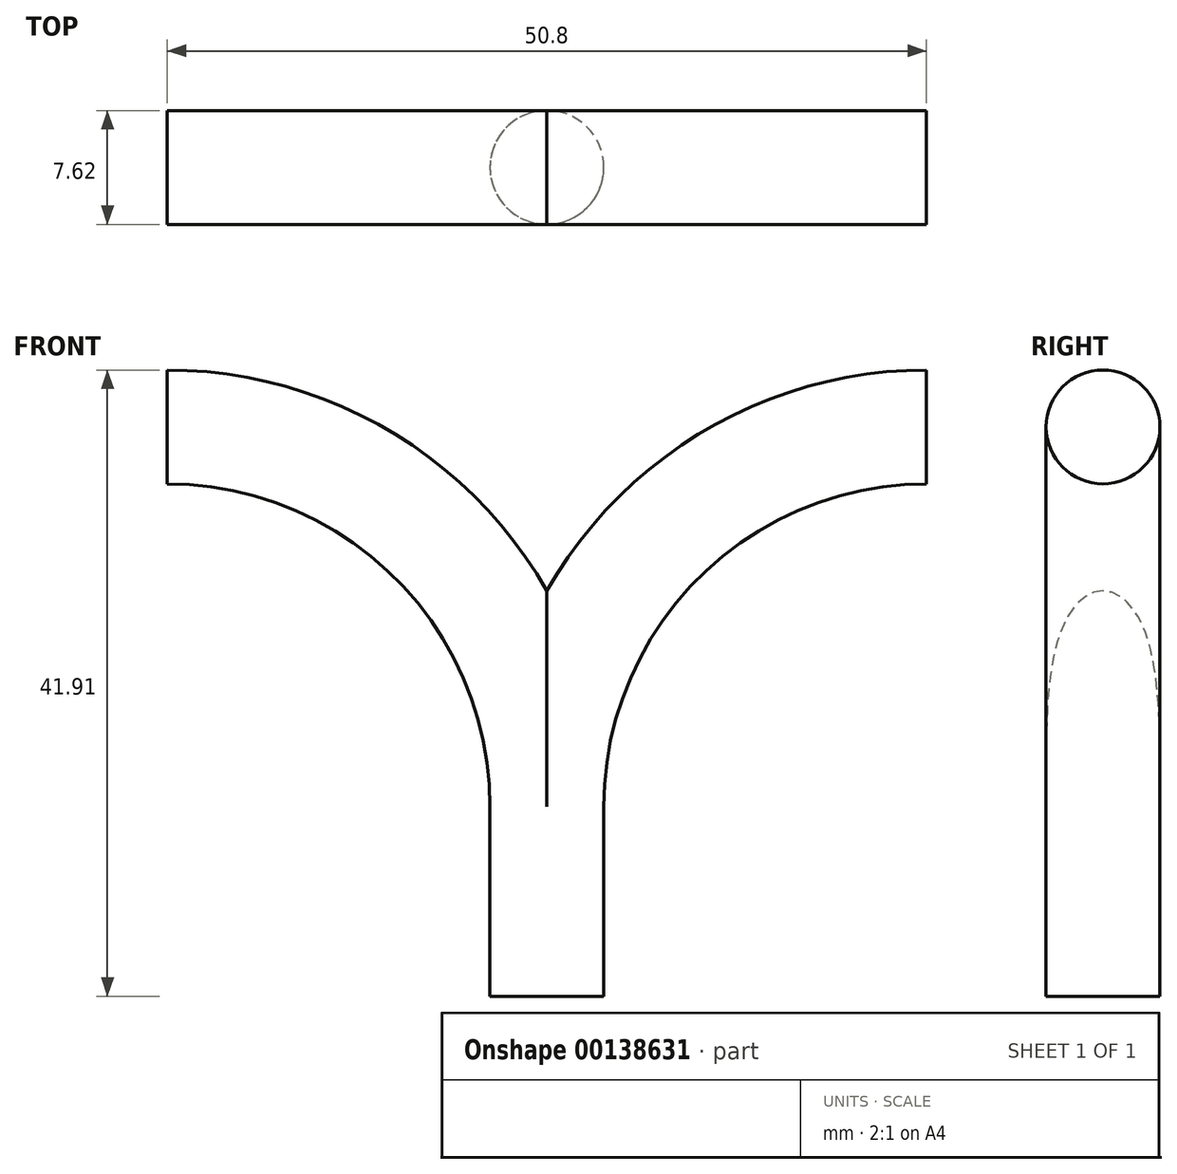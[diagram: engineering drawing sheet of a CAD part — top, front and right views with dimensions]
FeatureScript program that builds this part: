
annotation { "Feature Type Name" : "Feature", "Feature Type Description" : "" }
export const myFeature = defineFeature(function(context is Context, id is Id, definition is map)
    precondition{}
    {
        {
            var Q0;
            Q0=qCreatedBy(makeId("Top.planeOp"),FACE);
            var sketch = newSketch(context, id + "F0", { "sketchPlane" : qUnion([Q0])});
            skCircle(sketch, "E0", {"center": v(0, 0) * mm, "radius": 3.81 * mm});
            skSolve(sketch);
        }
        {
            var Q0;
            Q0=qCreatedBy(makeId("Front.planeOp"),FACE);
            var sketch = newSketch(context, id + "F1", { "sketchPlane" : qUnion([Q0])});
            skArc(sketch, "E1", {"start": v(0, 0) * mm, "mid": v(-7.44, 17.96) * mm, "end": v(-25.4, 25.4) * mm});
            skArc(sketch, "E2", {"start": v(25.4, 25.4) * mm, "mid": v(7.44, 17.96) * mm, "end": v(0, 0) * mm});
            skSolve(sketch);
        }
        {
            var Q0;
            Q0=makeQuery(id+"F0.imprint","IMPRINT",FACE,{"disambiguationData":[TD([[makeQuery(id+"F0.imprint","IMPRINT",EDGE,{"derivedFrom":sQuery(id+"F0.wireOp",EDGE,"E0")}),1.0]])]});
            var Q1;
            Q1=sQuery(id+"F1.wireOp",EDGE,"E2");
            sweep(context, id + "F2", {"profiles" : qUnion([Q0]), "path" : qUnion([Q1])});
        }
        {
            var Q0;
            Q0 = qSketchRegion(id + "F0", true);
            var Q1;
            Q1=sQuery(id+"F1.wireOp",EDGE,"E1");
            sweep(context, id + "F3", {"operationType" : NewBodyOperationType.ADD, "profiles" : qUnion([Q0]), "path" : qUnion([Q1])});
        }
        {
            var Q0;
            Q0=makeQuery(id+"F2.opSweep","CAP_FACE",FACE,{"disambiguationData":[OSD([sQuery(id+"F0.wireOp",EDGE,"E0"),sQuery(id+"F1.wireOp",VERTEX,"E2.end")])],"isStart":true});
            extrude(context, id + "F4", {"entities" : qUnion([Q0]), "operationType" : NewBodyOperationType.ADD, "depth" : 12.7 * mm});
        }
    });
